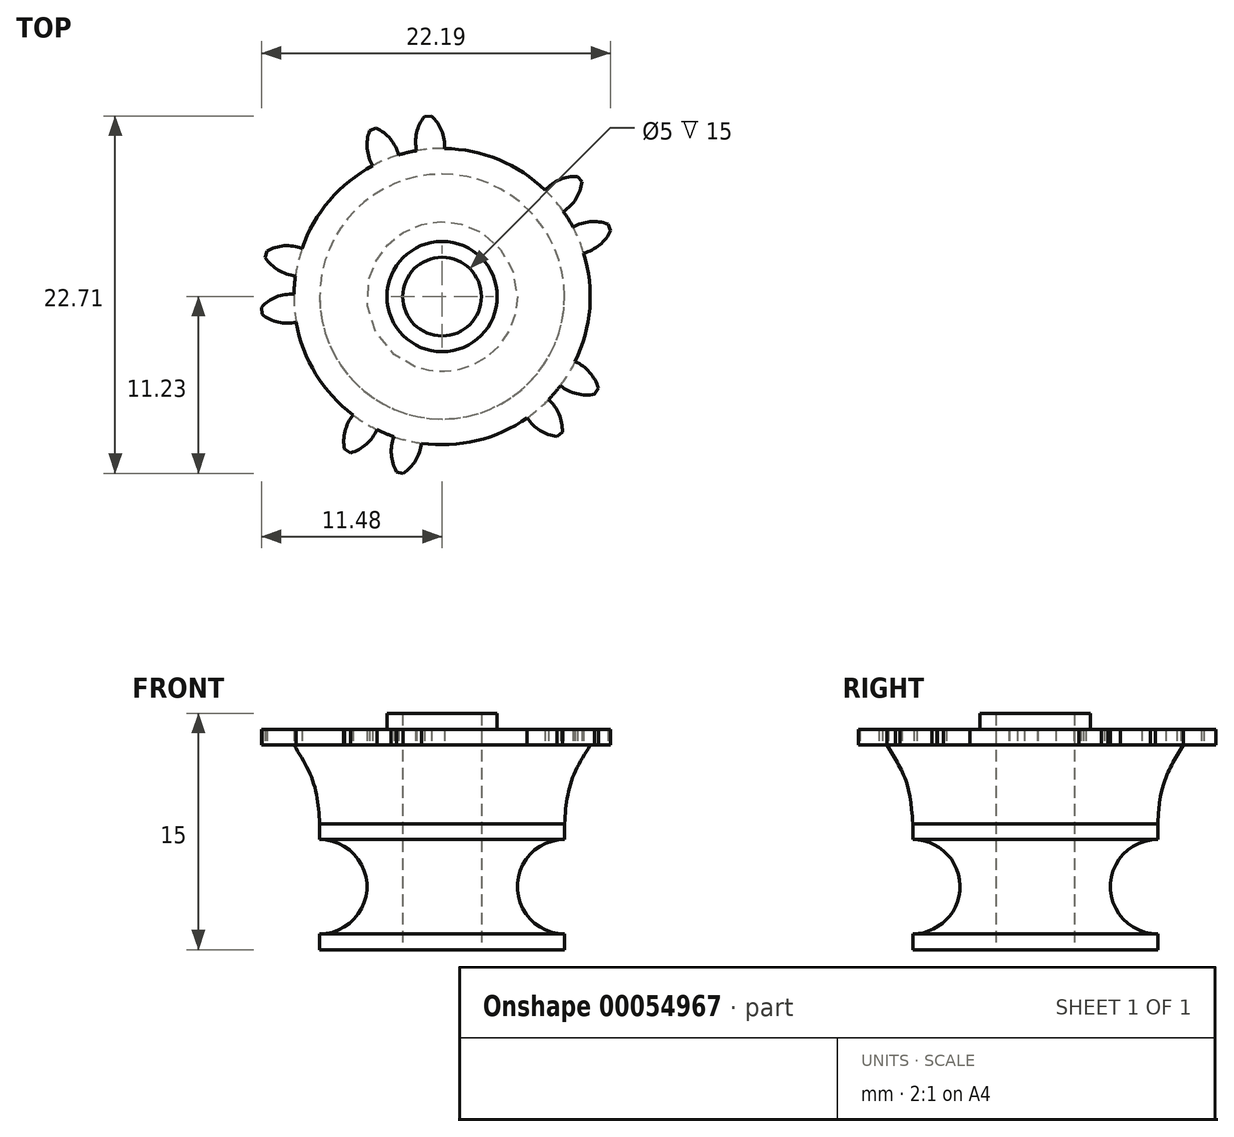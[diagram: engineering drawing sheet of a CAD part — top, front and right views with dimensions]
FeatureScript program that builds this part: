
annotation { "Feature Type Name" : "Feature", "Feature Type Description" : "" }
export const myFeature = defineFeature(function(context is Context, id is Id, definition is map)
    precondition{}
    {
        {
            assignVariable(context, id + "F0", {"name" : "GearDepth", "anyValue" : 1});
        }
        {
            var Q0;
            Q0=qCreatedBy(makeId("Top.planeOp"),FACE);
            var sketch = newSketch(context, id + "F1", { "sketchPlane" : qUnion([Q0])});
            skCircle(sketch, "E0", {"center": v(0, 0) * mm, "radius": 9.4 * mm});
            skCircle(sketch, "E1", {"center": v(0, 0) * mm, "radius": 10.45 * mm, "construction": true});
            skCircle(sketch, "E2", {"center": v(0, 0) * mm, "radius": 11.5 * mm, "construction": true});
            skLineSegment(sketch, "E3", {"start": v(0, 0) * mm, "end": v(0, 17.6) * mm, "construction": true});
            skLineSegment(sketch, "E4", {"start": v(0, 0) * mm, "end": v(-1.42, 18) * mm, "construction": true});
            skLineSegment(sketch, "E5", {"start": v(0, 10.45) * mm, "end": v(-10.54, 10.45) * mm, "construction": true});
            skLineSegment(sketch, "E6", {"start": v(0, 10.45) * mm, "end": v(-10.3, 6.7) * mm, "construction": true});
            skCircle(sketch, "E7", {"center": v(0, 10.45) * mm, "radius": 2.61 * mm, "construction": true});
            skCircle(sketch, "E8", {"center": v(-2.46, 9.56) * mm, "radius": 2.61 * mm, "construction": true});
            skArc(sketch, "E9", {"start": v(-4.91, 10.45) * mm, "mid": v(-4.92, 10.42) * mm, "end": v(-4.94, 10.39) * mm});
            skArc(sketch, "E10.trimOffspring", {"start": v(0.15, 9.4) * mm, "mid": v(-0.03, 10.54) * mm, "end": v(-0.68, 11.48) * mm});
            skArc(sketch, "E11.MirrorCS", {"start": v(-1.62, 9.27) * mm, "mid": v(-1.62, 10.41) * mm, "end": v(-1.12, 11.45) * mm});
            skLineSegment(sketch, "E12", {"start": v(-1.12, 11.45) * mm, "end": v(-0.68, 11.48) * mm});
            skArc(sketch, "E13.1.0", {"start": v(-2.76, 9) * mm, "mid": v(-3.29, 10.01) * mm, "end": v(-4.2, 10.7) * mm});
            skLineSegment(sketch, "E13.1.1", {"start": v(-4.6, 10.54) * mm, "end": v(-4.2, 10.7) * mm});
            skArc(sketch, "E13.1.2", {"start": v(-4.4, 8.31) * mm, "mid": v(-4.76, 9.4) * mm, "end": v(-4.6, 10.54) * mm});
            skArc(sketch, "E13.2.0", {"start": v(-5.4, 7.7) * mm, "mid": v(-6.22, 8.5) * mm, "end": v(-7.3, 8.89) * mm});
            skLineSegment(sketch, "E13.2.1", {"start": v(-7.64, 8.6) * mm, "end": v(-7.3, 8.89) * mm});
            skArc(sketch, "E13.2.2", {"start": v(-6.76, 6.54) * mm, "mid": v(-7.43, 7.47) * mm, "end": v(-7.64, 8.6) * mm});
            skArc(sketch, "E13.3.0", {"start": v(-7.52, 5.65) * mm, "mid": v(-8.54, 6.17) * mm, "end": v(-9.69, 6.2) * mm});
            skLineSegment(sketch, "E13.3.1", {"start": v(-9.92, 5.82) * mm, "end": v(-9.69, 6.2) * mm});
            skArc(sketch, "E13.3.2", {"start": v(-8.45, 4.13) * mm, "mid": v(-9.37, 4.81) * mm, "end": v(-9.92, 5.82) * mm});
            skArc(sketch, "E13.4.0", {"start": v(-8.9, 3.05) * mm, "mid": v(-10.03, 3.23) * mm, "end": v(-11.13, 2.9) * mm});
            skLineSegment(sketch, "E13.4.1", {"start": v(-11.23, 2.47) * mm, "end": v(-11.13, 2.9) * mm});
            skArc(sketch, "E13.4.2", {"start": v(-9.32, 1.32) * mm, "mid": v(-10.4, 1.68) * mm, "end": v(-11.23, 2.47) * mm});
            skArc(sketch, "E13.5.0", {"start": v(-9.4, 0.15) * mm, "mid": v(-10.54, -0.03) * mm, "end": v(-11.48, -0.68) * mm});
            skLineSegment(sketch, "E13.5.1", {"start": v(-11.45, -1.12) * mm, "end": v(-11.48, -0.68) * mm});
            skArc(sketch, "E13.5.2", {"start": v(-9.27, -1.62) * mm, "mid": v(-10.41, -1.62) * mm, "end": v(-11.45, -1.12) * mm});
            skArc(sketch, "E13.6.0", {"start": v(-9, -2.76) * mm, "mid": v(-10.01, -3.29) * mm, "end": v(-10.7, -4.2) * mm});
            skLineSegment(sketch, "E13.6.1", {"start": v(-10.54, -4.6) * mm, "end": v(-10.7, -4.2) * mm});
            skArc(sketch, "E13.6.2", {"start": v(-8.31, -4.4) * mm, "mid": v(-9.4, -4.76) * mm, "end": v(-10.54, -4.6) * mm});
            skArc(sketch, "E13.7.0", {"start": v(-7.7, -5.4) * mm, "mid": v(-8.5, -6.22) * mm, "end": v(-8.89, -7.3) * mm});
            skLineSegment(sketch, "E13.7.1", {"start": v(-8.6, -7.64) * mm, "end": v(-8.89, -7.3) * mm});
            skArc(sketch, "E13.7.2", {"start": v(-6.54, -6.76) * mm, "mid": v(-7.47, -7.43) * mm, "end": v(-8.6, -7.64) * mm});
            skArc(sketch, "E13.8.0", {"start": v(-5.65, -7.52) * mm, "mid": v(-6.17, -8.54) * mm, "end": v(-6.2, -9.69) * mm});
            skLineSegment(sketch, "E13.8.1", {"start": v(-5.82, -9.92) * mm, "end": v(-6.2, -9.69) * mm});
            skArc(sketch, "E13.8.2", {"start": v(-4.13, -8.45) * mm, "mid": v(-4.81, -9.37) * mm, "end": v(-5.82, -9.92) * mm});
            skArc(sketch, "E13.9.0", {"start": v(-3.05, -8.9) * mm, "mid": v(-3.23, -10.03) * mm, "end": v(-2.9, -11.13) * mm});
            skLineSegment(sketch, "E13.9.1", {"start": v(-2.47, -11.23) * mm, "end": v(-2.9, -11.13) * mm});
            skArc(sketch, "E13.9.2", {"start": v(-1.32, -9.32) * mm, "mid": v(-1.68, -10.4) * mm, "end": v(-2.47, -11.23) * mm});
            skArc(sketch, "E13.10.0", {"start": v(-0.15, -9.4) * mm, "mid": v(0.03, -10.54) * mm, "end": v(0.68, -11.48) * mm});
            skLineSegment(sketch, "E13.10.1", {"start": v(1.12, -11.45) * mm, "end": v(0.68, -11.48) * mm});
            skArc(sketch, "E13.10.2", {"start": v(1.62, -9.27) * mm, "mid": v(1.62, -10.41) * mm, "end": v(1.12, -11.45) * mm});
            skArc(sketch, "E13.11.0", {"start": v(2.76, -9) * mm, "mid": v(3.29, -10.01) * mm, "end": v(4.2, -10.7) * mm});
            skLineSegment(sketch, "E13.11.1", {"start": v(4.6, -10.54) * mm, "end": v(4.2, -10.7) * mm});
            skArc(sketch, "E13.11.2", {"start": v(4.4, -8.31) * mm, "mid": v(4.76, -9.4) * mm, "end": v(4.6, -10.54) * mm});
            skArc(sketch, "E13.12.0", {"start": v(5.4, -7.7) * mm, "mid": v(6.22, -8.5) * mm, "end": v(7.3, -8.89) * mm});
            skLineSegment(sketch, "E13.12.1", {"start": v(7.64, -8.6) * mm, "end": v(7.3, -8.89) * mm});
            skArc(sketch, "E13.12.2", {"start": v(6.76, -6.54) * mm, "mid": v(7.43, -7.47) * mm, "end": v(7.64, -8.6) * mm});
            skArc(sketch, "E13.13.0", {"start": v(7.52, -5.65) * mm, "mid": v(8.54, -6.17) * mm, "end": v(9.69, -6.2) * mm});
            skLineSegment(sketch, "E13.13.1", {"start": v(9.92, -5.82) * mm, "end": v(9.69, -6.2) * mm});
            skArc(sketch, "E13.13.2", {"start": v(8.45, -4.13) * mm, "mid": v(9.37, -4.81) * mm, "end": v(9.92, -5.82) * mm});
            skArc(sketch, "E13.14.0", {"start": v(8.9, -3.05) * mm, "mid": v(10.03, -3.23) * mm, "end": v(11.13, -2.9) * mm});
            skLineSegment(sketch, "E13.14.1", {"start": v(11.23, -2.47) * mm, "end": v(11.13, -2.9) * mm});
            skArc(sketch, "E13.14.2", {"start": v(9.32, -1.32) * mm, "mid": v(10.4, -1.68) * mm, "end": v(11.23, -2.47) * mm});
            skArc(sketch, "E13.15.0", {"start": v(9.4, -0.15) * mm, "mid": v(10.54, 0.03) * mm, "end": v(11.48, 0.68) * mm});
            skLineSegment(sketch, "E13.15.1", {"start": v(11.45, 1.12) * mm, "end": v(11.48, 0.68) * mm});
            skArc(sketch, "E13.15.2", {"start": v(9.27, 1.62) * mm, "mid": v(10.41, 1.62) * mm, "end": v(11.45, 1.12) * mm});
            skArc(sketch, "E13.16.0", {"start": v(9, 2.76) * mm, "mid": v(10.01, 3.29) * mm, "end": v(10.7, 4.2) * mm});
            skLineSegment(sketch, "E13.16.1", {"start": v(10.54, 4.6) * mm, "end": v(10.7, 4.2) * mm});
            skArc(sketch, "E13.16.2", {"start": v(8.31, 4.4) * mm, "mid": v(9.4, 4.76) * mm, "end": v(10.54, 4.6) * mm});
            skArc(sketch, "E13.17.0", {"start": v(7.7, 5.4) * mm, "mid": v(8.5, 6.22) * mm, "end": v(8.89, 7.3) * mm});
            skLineSegment(sketch, "E13.17.1", {"start": v(8.6, 7.64) * mm, "end": v(8.89, 7.3) * mm});
            skArc(sketch, "E13.17.2", {"start": v(6.54, 6.76) * mm, "mid": v(7.47, 7.43) * mm, "end": v(8.6, 7.64) * mm});
            skArc(sketch, "E13.18.0", {"start": v(5.65, 7.52) * mm, "mid": v(6.17, 8.54) * mm, "end": v(6.2, 9.69) * mm});
            skLineSegment(sketch, "E13.18.1", {"start": v(5.82, 9.92) * mm, "end": v(6.2, 9.69) * mm});
            skArc(sketch, "E13.18.2", {"start": v(4.13, 8.45) * mm, "mid": v(4.81, 9.37) * mm, "end": v(5.82, 9.92) * mm});
            skArc(sketch, "E13.19.0", {"start": v(3.05, 8.9) * mm, "mid": v(3.23, 10.03) * mm, "end": v(2.9, 11.13) * mm});
            skLineSegment(sketch, "E13.19.1", {"start": v(2.47, 11.23) * mm, "end": v(2.9, 11.13) * mm});
            skArc(sketch, "E13.19.2", {"start": v(1.32, 9.32) * mm, "mid": v(1.68, 10.4) * mm, "end": v(2.47, 11.23) * mm});
            skCircle(sketch, "E14", {"center": v(0, 0) * mm, "radius": 2.5 * mm});
            skCircle(sketch, "E15", {"center": v(0, 0) * mm, "radius": 3.5 * mm});
            skSolve(sketch);
        }
        {
            var Q0;
            {var subQ0=sQuery(id+"F1.wireOp",EDGE,"E10.trimOffspring");Q0=makeQuery(id+"F1.imprint","IMPRINT",FACE,{"disambiguationData":[TD([[makeQuery(id+"F1.imprint","IMPRINT",EDGE,{"derivedFrom":subQ0}),1.0]])]});}
            var Q1;
            {var subQ0=sQuery(id+"F1.wireOp",EDGE,"E0");var subQ1=makeQuery(id+"F1.imprint","INTERSECT",VERTEX,{"derivedFrom":[subQ0,sQuery(id+"F1.wireOp",EDGE,"E10.trimOffspring")]});Q1=makeQuery(id+"F1.imprint","IMPRINT",FACE,{"disambiguationData":[TD([[makeQuery(id+"F1.imprint","IMPRINT",EDGE,{"disambiguationData":[TD([[subQ1,-1.0]])],"derivedFrom":subQ0}),1.0]])]});}
            var Q2;
            {var subQ0=sQuery(id+"F1.wireOp",EDGE,"E13.1.0");Q2=makeQuery(id+"F1.imprint","IMPRINT",FACE,{"disambiguationData":[TD([[makeQuery(id+"F1.imprint","IMPRINT",EDGE,{"derivedFrom":subQ0}),1.0]])]});}
            var Q3;
            {var subQ0=sQuery(id+"F1.wireOp",EDGE,"E13.4.0");Q3=makeQuery(id+"F1.imprint","IMPRINT",FACE,{"disambiguationData":[TD([[makeQuery(id+"F1.imprint","IMPRINT",EDGE,{"derivedFrom":subQ0}),1.0]])]});}
            var Q4;
            {var subQ0=sQuery(id+"F1.wireOp",EDGE,"E13.5.0");Q4=makeQuery(id+"F1.imprint","IMPRINT",FACE,{"disambiguationData":[TD([[makeQuery(id+"F1.imprint","IMPRINT",EDGE,{"derivedFrom":subQ0}),1.0]])]});}
            var Q5;
            {var subQ0=sQuery(id+"F1.wireOp",EDGE,"E13.8.0");Q5=makeQuery(id+"F1.imprint","IMPRINT",FACE,{"disambiguationData":[TD([[makeQuery(id+"F1.imprint","IMPRINT",EDGE,{"derivedFrom":subQ0}),1.0]])]});}
            var Q6;
            {var subQ0=sQuery(id+"F1.wireOp",EDGE,"E13.9.0");Q6=makeQuery(id+"F1.imprint","IMPRINT",FACE,{"disambiguationData":[TD([[makeQuery(id+"F1.imprint","IMPRINT",EDGE,{"derivedFrom":subQ0}),1.0]])]});}
            var Q7;
            {var subQ0=sQuery(id+"F1.wireOp",EDGE,"E13.12.0");Q7=makeQuery(id+"F1.imprint","IMPRINT",FACE,{"disambiguationData":[TD([[makeQuery(id+"F1.imprint","IMPRINT",EDGE,{"derivedFrom":subQ0}),1.0]])]});}
            var Q8;
            {var subQ0=sQuery(id+"F1.wireOp",EDGE,"E13.13.0");Q8=makeQuery(id+"F1.imprint","IMPRINT",FACE,{"disambiguationData":[TD([[makeQuery(id+"F1.imprint","IMPRINT",EDGE,{"derivedFrom":subQ0}),1.0]])]});}
            var Q9;
            {var subQ0=sQuery(id+"F1.wireOp",EDGE,"E13.16.0");Q9=makeQuery(id+"F1.imprint","IMPRINT",FACE,{"disambiguationData":[TD([[makeQuery(id+"F1.imprint","IMPRINT",EDGE,{"derivedFrom":subQ0}),1.0]])]});}
            var Q10;
            {var subQ0=sQuery(id+"F1.wireOp",EDGE,"E13.17.0");Q10=makeQuery(id+"F1.imprint","IMPRINT",FACE,{"disambiguationData":[TD([[makeQuery(id+"F1.imprint","IMPRINT",EDGE,{"derivedFrom":subQ0}),1.0]])]});}
            var Q11;
            Q11=makeQuery(id+"F1.imprint","IMPRINT",FACE,{"disambiguationData":[TD([[makeQuery(id+"F1.imprint","IMPRINT",EDGE,{"derivedFrom":sQuery(id+"F1.wireOp",EDGE,"E15")}),-1.0]])]});
            var Q12;
            Q12=makeQuery(id+"F1.imprint","IMPRINT",FACE,{"disambiguationData":[TD([[makeQuery(id+"F1.imprint","IMPRINT",EDGE,{"derivedFrom":sQuery(id+"F1.wireOp",EDGE,"E14")}),-1.0]])]});
            var Q13;
            Q13=makeQuery(id+"F1.imprint","IMPRINT",FACE,{"disambiguationData":[TD([[makeQuery(id+"F1.imprint","IMPRINT",EDGE,{"derivedFrom":sQuery(id+"F1.wireOp",EDGE,"f8a4fba6-3b89-41ba-ad4d-dba6b573ff57")}),-1.0]])]});
            var Q14;
            Q14=sQuery(id+"F1.wireOp",EDGE,"E0");
            var Q15;
            Q15=sQuery(id+"F1.wireOp",EDGE,"E10.trimOffspring");
            var Q16;
            Q16=sQuery(id+"F1.wireOp",EDGE,"E12");
            var Q17;
            Q17=sQuery(id+"F1.wireOp",EDGE,"E11.MirrorCS");
            extrude(context, id + "F2", {"entities" : qUnion([Q0, Q1, Q2, Q3, Q4, Q5, Q6, Q7, Q8, Q9, Q10, Q11, Q12, Q13]), "surfaceEntities" : qUnion([Q14, Q15, Q16, Q17]), "depth" : (getVariable(context, 'GearDepth')) * mm});
        }
        {
            var Q0;
            Q0=makeQuery(id+"F1.imprint","IMPRINT",FACE,{"disambiguationData":[TD([[makeQuery(id+"F1.imprint","IMPRINT",EDGE,{"derivedFrom":sQuery(id+"F1.wireOp",EDGE,"E14")}),-1.0]])]});
            extrude(context, id + "F3", {"entities" : qUnion([Q0]), "operationType" : NewBodyOperationType.ADD, "depth" : 2 * mm});
        }
        {
            var Q0;
            Q0=makeQuery(id+"F1.imprint","IMPRINT",FACE,{"disambiguationData":[TD([[makeQuery(id+"F1.imprint","IMPRINT",EDGE,{"derivedFrom":sQuery(id+"F1.wireOp",EDGE,"E15")}),-1.0]])]});
            cPlane(context, id + "F4", {"entities" : qUnion([Q0]), "cplaneType" : CPlaneType.OFFSET, "offset" : 6 * mm, "oppositeDirection" : true, "width" : 150 * mm, "height" : 150 * mm});
        }
        {
            var Q0;
            Q0=qCreatedBy(id+"F4.planeOp",FACE);
            var sketch = newSketch(context, id + "F5", { "sketchPlane" : qUnion([Q0])});
            skCircle(sketch, "E16", {"center": v(0, 0) * mm, "radius": 4.77 * mm});
            skCircle(sketch, "E17", {"center": v(0, 0) * mm, "radius": 7.77 * mm});
            skCircle(sketch, "E18", {"center": v(0, 0) * mm, "radius": 2.5 * mm});
            skSolve(sketch);
        }
        {
            var Q0;
            Q0=makeQuery(id+"F5.imprint","IMPRINT",FACE,{"disambiguationData":[TD([[makeQuery(id+"F5.imprint","IMPRINT",EDGE,{"derivedFrom":sQuery(id+"F5.wireOp",EDGE,"E16")}),1.0]])]});
            var Q1;
            Q1=makeQuery(id+"F2.opExtrude","CAP_FACE",FACE,{"disambiguationData":[OSD([sQuery(id+"F1.wireOp",EDGE,"E0"),sQuery(id+"F1.wireOp",EDGE,"E10.trimOffspring"),sQuery(id+"F1.wireOp",EDGE,"E11.MirrorCS"),sQuery(id+"F1.wireOp",EDGE,"E12"),sQuery(id+"F1.wireOp",EDGE,"E13.1.0"),sQuery(id+"F1.wireOp",EDGE,"E13.1.1"),sQuery(id+"F1.wireOp",EDGE,"E13.1.2"),sQuery(id+"F1.wireOp",EDGE,"E13.4.0"),sQuery(id+"F1.wireOp",EDGE,"E13.4.1"),sQuery(id+"F1.wireOp",EDGE,"E13.4.2"),sQuery(id+"F1.wireOp",EDGE,"E13.5.0"),sQuery(id+"F1.wireOp",EDGE,"E13.5.1"),sQuery(id+"F1.wireOp",EDGE,"E13.5.2"),sQuery(id+"F1.wireOp",EDGE,"E13.8.0"),sQuery(id+"F1.wireOp",EDGE,"E13.8.1"),sQuery(id+"F1.wireOp",EDGE,"E13.8.2"),sQuery(id+"F1.wireOp",EDGE,"E13.9.0"),sQuery(id+"F1.wireOp",EDGE,"E13.9.1"),sQuery(id+"F1.wireOp",EDGE,"E13.9.2"),sQuery(id+"F1.wireOp",EDGE,"E13.12.0"),sQuery(id+"F1.wireOp",EDGE,"E13.12.1"),sQuery(id+"F1.wireOp",EDGE,"E13.12.2"),sQuery(id+"F1.wireOp",EDGE,"E13.13.0"),sQuery(id+"F1.wireOp",EDGE,"E13.13.1"),sQuery(id+"F1.wireOp",EDGE,"E13.13.2"),sQuery(id+"F1.wireOp",EDGE,"E13.16.0"),sQuery(id+"F1.wireOp",EDGE,"E13.16.1"),sQuery(id+"F1.wireOp",EDGE,"E13.16.2"),sQuery(id+"F1.wireOp",EDGE,"E13.17.0"),sQuery(id+"F1.wireOp",EDGE,"E13.17.1"),sQuery(id+"F1.wireOp",EDGE,"E13.17.2"),sQuery(id+"F1.wireOp",EDGE,"E14")])],"isStart":true});
            extrude(context, id + "F6", {"entities" : qUnion([Q0]), "operationType" : NewBodyOperationType.ADD, "endBound" : BoundingType.UP_TO_SURFACE, "endBoundEntityFace" : qUnion([Q1]), "depth" : 25 * mm});
        }
        {
            var Q0;
            Q0=makeQuery(id+"F5.imprint","IMPRINT",FACE,{"disambiguationData":[TD([[makeQuery(id+"F5.imprint","IMPRINT",EDGE,{"derivedFrom":sQuery(id+"F5.wireOp",EDGE,"E16")}),-1.0]])]});
            extrude(context, id + "F7", {"entities" : qUnion([Q0]), "operationType" : NewBodyOperationType.ADD, "depth" : 1 * mm});
        }
        {
            var Q0;
            Q0=makeQuery(id+"F5.imprint","IMPRINT",FACE,{"disambiguationData":[TD([[makeQuery(id+"F5.imprint","IMPRINT",EDGE,{"derivedFrom":sQuery(id+"F5.wireOp",EDGE,"E16")}),1.0]])]});
            extrude(context, id + "F8", {"entities" : qUnion([Q0]), "operationType" : NewBodyOperationType.ADD, "oppositeDirection" : true, "depth" : 6 * mm});
        }
        {
            var Q0;
            Q0=makeQuery(id+"F8.opExtrude","CAP_FACE",FACE,{"disambiguationData":[OSD([sQuery(id+"F5.wireOp",EDGE,"E16"),sQuery(id+"F5.wireOp",EDGE,"E18")])],"isStart":false});
            var sketch = newSketch(context, id + "F9", { "sketchPlane" : qUnion([Q0])});
            skCircle(sketch, "E19", {"center": v(0, 0) * mm, "radius": 7.77 * mm});
            skSolve(sketch);
        }
        {
            var Q0;
            Q0=makeQuery(id+"F9.imprint","IMPRINT",FACE,{"disambiguationData":[TD([[makeQuery(id+"F9.imprint","IMPRINT",EDGE,{"derivedFrom":sQuery(id+"F9.wireOp",EDGE,"E19")}),1.0]])]});
            var Q1;
            Q1=makeQuery(id+"F9.imprint","IMPRINT",FACE,{"disambiguationData":[TD([[makeQuery(id+"F9.imprint","IMPRINT",EDGE,{"derivedFrom":makeQuery(id+"F8.opExtrude","CAP_EDGE",EDGE,{"disambiguationData":[OSD([sQuery(id+"F5.wireOp",EDGE,"E16")])],"isStart":false})}),-1.0]])]});
            extrude(context, id + "F10", {"entities" : qUnion([Q0, Q1]), "operationType" : NewBodyOperationType.ADD, "depth" : 1 * mm});
        }
        {
            var Q0;
            Q0=qCreatedBy(makeId("Front.planeOp"),FACE);
            var sketch = newSketch(context, id + "F11", { "sketchPlane" : qUnion([Q0])});
            skLineSegment(sketch, "E20", {"start": v(0, -6.32) * mm, "end": v(0, -12.02) * mm, "construction": true});
            skLineSegment(sketch, "E21", {"start": v(4.77, -6) * mm, "end": v(4.77, -12) * mm});
            skLineSegment(sketch, "E22", {"start": v(4.77, -12) * mm, "end": v(7.77, -12) * mm});
            skLineSegment(sketch, "E23", {"start": v(4.77, -6) * mm, "end": v(7.77, -6) * mm});
            skArc(sketch, "E24", {"start": v(7.77, -6) * mm, "mid": v(4.77, -9) * mm, "end": v(7.77, -12) * mm});
            skLineSegment(sketch, "E25", {"start": v(9.4, 0) * mm, "end": v(4.77, 0) * mm});
            skLineSegment(sketch, "E26", {"start": v(4.77, 0) * mm, "end": v(4.77, -5) * mm});
            skLineSegment(sketch, "E27", {"start": v(4.77, -5) * mm, "end": v(7.77, -5) * mm});
            skFitSpline(sketch, "E28", {"points": [v(7.77, -5) * mm, v(8.17, -2.42) * mm, v(9.4, 0) * mm], "startDerivative": vector(0.4, 5.36) * mm, "endDerivative": vector(2.89, 4.7) * mm});
            skSolve(sketch);
        }
        {
            var Q0;
            {var subQ0=sQuery(id+"F11.wireOp",EDGE,"E23");Q0=makeQuery(id+"F11.imprint","IMPRINT",FACE,{"disambiguationData":[TD([[makeQuery(id+"F11.imprint","IMPRINT",EDGE,{"derivedFrom":subQ0}),-1.0]])]});}
            var Q1;
            {var subQ0=sQuery(id+"F11.wireOp",EDGE,"E22");Q1=makeQuery(id+"F11.imprint","IMPRINT",FACE,{"disambiguationData":[TD([[makeQuery(id+"F11.imprint","IMPRINT",EDGE,{"derivedFrom":subQ0}),1.0]])]});}
            var Q2;
            Q2=makeQuery(id+"F11.imprint","IMPRINT",FACE,{"disambiguationData":[TD([[makeQuery(id+"F11.imprint","IMPRINT",EDGE,{"derivedFrom":sQuery(id+"F11.wireOp",EDGE,"E25")}),1.0]])]});
            var Q3;
            Q3=sQuery(id+"F11.wireOp",EDGE,"E20");
            revolve(context, id + "F12", {"operationType" : NewBodyOperationType.ADD, "entities" : qUnion([Q0, Q1, Q2]), "axis" : qUnion([Q3]), "revolveType" : RevolveType.FULL});
        }
    });
